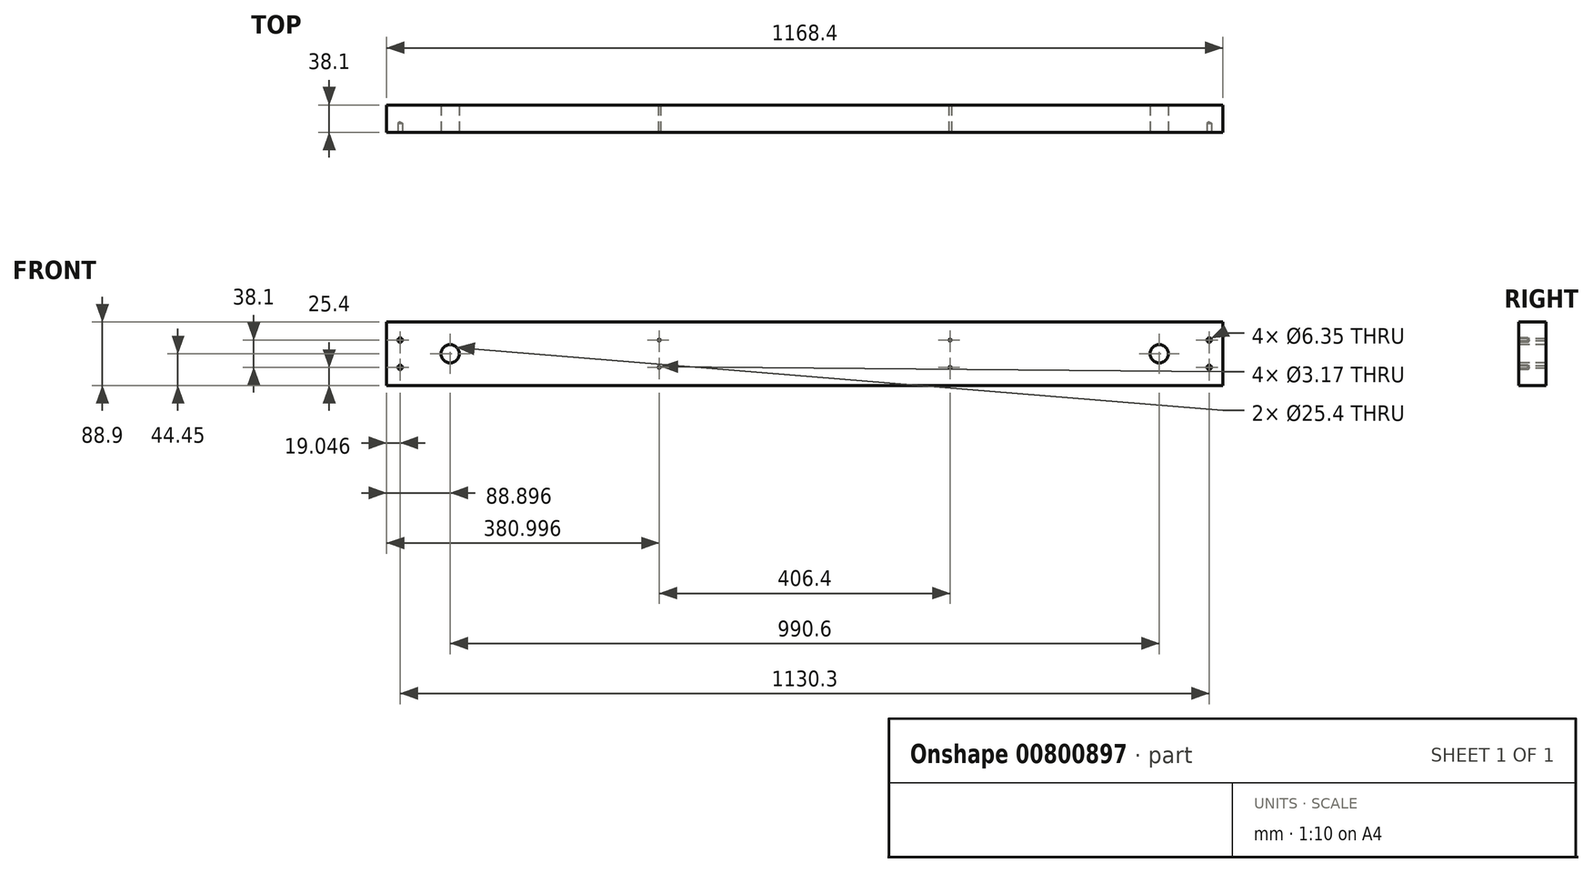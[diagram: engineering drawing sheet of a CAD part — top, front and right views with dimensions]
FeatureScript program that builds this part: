
annotation { "Feature Type Name" : "Feature", "Feature Type Description" : "" }
export const myFeature = defineFeature(function(context is Context, id is Id, definition is map)
    precondition{}
    {
        {
            var Q0;
            Q0=qCreatedBy(makeId("Front.planeOp"),FACE);
            var sketch = newSketch(context, id + "F0", { "sketchPlane" : qUnion([Q0])});
            skLineSegment(sketch, "E0.bottom", {"start": v(-634.12, 63.36) * mm, "end": v(534.28, 63.36) * mm});
            skLineSegment(sketch, "E0.top", {"start": v(-634.12, -25.54) * mm, "end": v(534.28, -25.54) * mm});
            skLineSegment(sketch, "E0.left", {"start": v(-634.12, 63.36) * mm, "end": v(-634.12, -25.54) * mm});
            skLineSegment(sketch, "E0.right", {"start": v(534.28, 63.36) * mm, "end": v(534.28, -25.54) * mm});
            skSolve(sketch);
        }
        {
            var Q0;
            Q0=makeQuery(id+"F0.imprint","IMPRINT",FACE,{"disambiguationData":[TD([[makeQuery(id+"F0.imprint","IMPRINT",EDGE,{"derivedFrom":sQuery(id+"F0.wireOp",EDGE,"E0.bottom")}),-1.0]])]});
            extrude(context, id + "F1", {"entities" : qUnion([Q0]), "depth" : 38.1 * mm, "offsetDistance" : 25.4 * mm});
        }
        {
            var Q0;
            Q0=makeQuery(id+"F1.opExtrude","CAP_FACE",FACE,{"disambiguationData":[OSD([sQuery(id+"F0.wireOp",EDGE,"E0.bottom"),sQuery(id+"F0.wireOp",EDGE,"E0.top"),sQuery(id+"F0.wireOp",EDGE,"E0.left"),sQuery(id+"F0.wireOp",EDGE,"E0.right")])],"isStart":false});
            var sketch = newSketch(context, id + "F2", { "sketchPlane" : qUnion([Q0])});
            skLineSegment(sketch, "E1", {"start": v(-49.92, -25.54) * mm, "end": v(-49.92, 63.36) * mm, "construction": true});
            skLineSegment(sketch, "E2", {"start": v(515.23, 63.36) * mm, "end": v(515.23, -25.54) * mm, "construction": true});
            skPoint(sketch, "E3", {"position": v(515.23, 37.96) * mm});
            skPoint(sketch, "E4", {"position": v(515.23, -0.14) * mm});
            skPoint(sketch, "E5.MirrorP", {"position": v(-615.07, 37.96) * mm});
            skPoint(sketch, "E6.MirrorP", {"position": v(-615.07, -0.14) * mm});
            skSolve(sketch);
        }
        {
            var Q0;
            Q0=sQuery(id+"F2.wireOp",VERTEX,"E3");
            var Q1;
            Q1=sQuery(id+"F2.wireOp",VERTEX,"E4");
            var Q2;
            Q2=sQuery(id+"F2.wireOp",VERTEX,"E5.MirrorP");
            var Q3;
            Q3=sQuery(id+"F2.wireOp",VERTEX,"E6.MirrorP");
            var Q4;
            Q4=makeQuery(id+"F1.opExtrude","SWEPT_BODY",BODY,{"disambiguationData":[OSD([sQuery(id+"F0.wireOp",EDGE,"E0.bottom"),sQuery(id+"F0.wireOp",EDGE,"E0.top"),sQuery(id+"F0.wireOp",EDGE,"E0.left"),sQuery(id+"F0.wireOp",EDGE,"E0.right")])]});
            hole(context, id + "F3", {"style" : HoleStyle.SIMPLE, "endStyle" : HoleEndStyle.BLIND, "holeDiameter" : 6.35 * mm, "majorDiameter" : 6.35 * mm, "holeDepth" : 12.7 * mm, "isTappedThrough" : true, "tappedDepth" : 12.7 * mm, "tapClearance" : 3, "locations" : qUnion([Q0, Q1, Q2, Q3]), "scope" : qUnion([Q4])});
        }
        {
            var Q0;
            Q0=makeQuery(id+"F1.opExtrude","CAP_FACE",FACE,{"disambiguationData":[OSD([sQuery(id+"F0.wireOp",EDGE,"E0.bottom"),sQuery(id+"F0.wireOp",EDGE,"E0.top"),sQuery(id+"F0.wireOp",EDGE,"E0.left"),sQuery(id+"F0.wireOp",EDGE,"E0.right")])],"isStart":false});
            var sketch = newSketch(context, id + "F4", { "sketchPlane" : qUnion([Q0])});
            skLineSegment(sketch, "E7", {"start": v(-634.12, 18.91) * mm, "end": v(-370.31, 18.91) * mm, "construction": true});
            skPoint(sketch, "E7.startSnap0", {"position": v(-634.12, 18.91) * mm});
            skPoint(sketch, "E8", {"position": v(-545.22, 18.91) * mm});
            skLineSegment(sketch, "E9", {"start": v(-49.92, 63.36) * mm, "end": v(-49.92, -25.54) * mm, "construction": true});
            skPoint(sketch, "E10.MirrorP", {"position": v(445.38, 18.91) * mm});
            skSolve(sketch);
        }
        {
            var Q0;
            Q0=sQuery(id+"F4.wireOp",VERTEX,"E8");
            var Q1;
            Q1=sQuery(id+"F4.wireOp",VERTEX,"E10.MirrorP");
            var Q2;
            Q2=makeQuery(id+"F1.opExtrude","SWEPT_BODY",BODY,{"disambiguationData":[OSD([sQuery(id+"F0.wireOp",EDGE,"E0.bottom"),sQuery(id+"F0.wireOp",EDGE,"E0.top"),sQuery(id+"F0.wireOp",EDGE,"E0.left"),sQuery(id+"F0.wireOp",EDGE,"E0.right")])]});
            hole(context, id + "F5", {"style" : HoleStyle.SIMPLE, "endStyle" : HoleEndStyle.THROUGH, "holeDiameter" : 25.4 * mm, "majorDiameter" : 6.35 * mm, "isTappedThrough" : true, "tappedDepth" : 12.7 * mm, "tapClearance" : 3, "locations" : qUnion([Q0, Q1]), "scope" : qUnion([Q2])});
        }
        {
            var Q0;
            Q0=makeQuery(id+"F1.opExtrude","CAP_FACE",FACE,{"disambiguationData":[OSD([sQuery(id+"F0.wireOp",EDGE,"E0.bottom"),sQuery(id+"F0.wireOp",EDGE,"E0.top"),sQuery(id+"F0.wireOp",EDGE,"E0.left"),sQuery(id+"F0.wireOp",EDGE,"E0.right")])],"isStart":false});
            var sketch = newSketch(context, id + "F6", { "sketchPlane" : qUnion([Q0])});
            skLineSegment(sketch, "E11", {"start": v(-253.12, -25.54) * mm, "end": v(-253.12, 63.36) * mm, "construction": true});
            skLineSegment(sketch, "E12", {"start": v(153.28, -25.54) * mm, "end": v(153.28, 63.36) * mm, "construction": true});
            skPoint(sketch, "E13", {"position": v(-253.12, 37.96) * mm});
            skPoint(sketch, "E14", {"position": v(-253.12, -0.14) * mm});
            skPoint(sketch, "E15", {"position": v(153.28, 37.96) * mm});
            skPoint(sketch, "E16", {"position": v(153.28, -0.14) * mm});
            skSolve(sketch);
        }
        {
            var Q0;
            Q0=sQuery(id+"F6.wireOp",VERTEX,"E13");
            var Q1;
            Q1=sQuery(id+"F6.wireOp",VERTEX,"E14");
            var Q2;
            Q2=sQuery(id+"F6.wireOp",VERTEX,"E15");
            var Q3;
            Q3=sQuery(id+"F6.wireOp",VERTEX,"E16");
            var Q4;
            Q4=makeQuery(id+"F1.opExtrude","SWEPT_BODY",BODY,{"disambiguationData":[OSD([sQuery(id+"F0.wireOp",EDGE,"E0.bottom"),sQuery(id+"F0.wireOp",EDGE,"E0.top"),sQuery(id+"F0.wireOp",EDGE,"E0.left"),sQuery(id+"F0.wireOp",EDGE,"E0.right")])]});
            hole(context, id + "F7", {"style" : HoleStyle.SIMPLE, "endStyle" : HoleEndStyle.THROUGH, "holeDiameter" : 3.17 * mm, "majorDiameter" : 6.35 * mm, "isTappedThrough" : true, "tappedDepth" : 12.7 * mm, "tapClearance" : 3, "locations" : qUnion([Q0, Q1, Q2, Q3]), "scope" : qUnion([Q4])});
        }
    });
